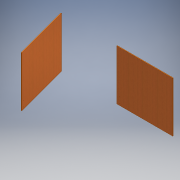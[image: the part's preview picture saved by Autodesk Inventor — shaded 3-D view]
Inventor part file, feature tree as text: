
AUTODESK INVENTOR PART (.ipt)
format: ipt  version: 2016 (Build 200138000, 138)  size: 173,568 bytes
history: native  units: mm
features: extrude x4, sketch x4, projected_geometry x2, plane x1
ambient origin geometry x8: Origin, YZ Plane, XZ Plane, XY Plane, X Axis, Y Axis, Z Axis, Center Point
bodies: Solid1 (feature_tree)
feature tree (11):
  plane  "Plano de trabajo4"
  extrude  "Extrusión8"  Depth=721.666667mm
  extrude  "Extrusión9"  TaperAngle=0.0deg  [1 undecoded]
  extrude  "Extrusión10"  Depth=80.0mm
  extrude  "Extrusión11"  Depth=730.0mm
  sketch  "Boceto8"  dims[d38=290.0mm d39=721.666667mm]
  sketch  "Boceto9"  dims[d40=10.0mm d42=0.0mm]
  projected_geometry  "Contorno proyectado7"
  sketch  "Boceto10"  dims[d43=36.083333mm d44=80.0mm]
  sketch  "Boceto11"  dims[d45=6.0mm d46=50.0mm d47=740.0mm d48=0.0mm d49=721.666667mm d50=721.666667mm d52=10.0mm d53=721.666667mm d54=730.0mm d55=0.0mm d56=36.083333mm d57=80.0mm d58=6.0mm d59=50.0mm d60=730.0mm d61=0.0mm]
  projected_geometry  "Contorno proyectado8"
note: 1 required parameter value undecoded (feature->parameter linkage not recoverable at this tier; creation-order binding heuristic only, values carry confidence <= 0.55)
